# Revit family: 05-2703-14-14
name_source: partatom
category: Luminarias
revit_build: Autodesk Revit 2017 (Build: 20160225_1515(x64)
units: mm (PartAtom-declared; Revit-internal decimal feet)

## family parameters
Anfitrión = Cara
Compartido = Sí
Corte con vacíos al cargar = No
Cota de conector redondo = Diámetro de uso
Número OmniClass = 23.80.70.00
Origen de luz = No
Punto de cálculo de habitación = No
Tipo de pieza = Normal
Título OmniClass = Lighting

## types (1)
- 05-2703-14-14
    Acabado = Blanco, Opal
    CRI = 80
    Carga aparente = 0 VA
    Catálogo = Decorative
    CodigoGubimclass = 50.60.50.20
    CodigoOmniclass = 21-04 50 40
    CodigoUniclass2015 = EF_70_80
    CodigoUniformat2010 = D5040
    DescripcionGubimclass = Iluminación interior
    DescripcionOmniclass = Lighting
    DescripcionUniclass2015 = Lighting
    DescripcionUniformat2010 = Lighting
    EAN13 = 8435381423872
    Eficiencia energética = LED A++
    Elevación por defecto = 1000 mm  [stored 3.28084 ft]
    Etiqueta V/f = 100-240V/50-60Hz
    Fabricante = LEDS C4
    Familia = Lia LED 250mm
    FechaVersion = Julio 2020
    Ficha = http://files.leds-c4.com
    Fotometría = http://files.leds-c4.com
    Fuente de luz = 18xLED 6.7 630.00 lm
    IMC = http://files.leds-c4.com
    IP = IP20
    IfcExportAs = IfcLightFixture
IfcLightFixture
    IfcExportType = NOTDEFINED
    Imagen web = http://files.leds-c4.com
    LDT = http://files.leds-c4.com
    Lumenes reales (lm) = 544
    Material = Acero, Policarbonato
    Peso neto (KG) = 0.68
    Pluma comercial = http://files.leds-c4.com
    Producto descatalogado = Catalogado ES
    Rayo de luz = HORIZONTAL
    Referencia = 05-2703-14-14
    Temperatura color led (K) = Blanco cálido - 3000K
    Tender text (Castellano) = LEDS C4
Lia LED 250mm
05-2703-14-14V1

Aplique de uso interior para iluminar frontalmente y hacia abajo. 

Diseño atemporal. Muy versátil. Múltiples instalaciones. Alto rendimiento W/lm reales. Òptimo precio-rendimiento. Fácil instalación. Alta durabilidad para uso intensivo. Material estructura: Acero. Acabado estructura: Blanco. Material difusor: Policarbonato. Acabado difusor: Opal. Garantía: 5 Años.

Peso neto del producto (Kg): 0.680
Anchura o diámetro del producto (mm): 250
Altura del producto (mm): 50
Salida del producto (mm): 80

Clase 2. Prueba hilo incandescente: 960. IP: IP20. LED. Nº de portalámparas o Leds: 18. Marca del LED: SEOUL. Marca del Driver: SELF. Potencia máxima de la fuente de luz: 6.7W. Temperatura de color: Blanco cálido - 3000K. Índice de reproducción cromática: 80. Steps Mac Adam: 3. Diámetro máximo de la bombilla que admite la luminaria: 50.000h L80B20. UGR:  12.2. Riesgo fotobiológico: RG0. Flujo real (lm): 544. Flujo nominal (lm): 630. Lm/W reales: 62. Rango de voltaje/frecuencia: 100-240. Voltaje: 3. Equipo incluido: Si, electrónico. Equipo multivoltaje incluido. Potencia total: 8.8. Factor de potencia: 0.52.
    Tender text (English) = LEDS C4
Lia LED 250mm
05-2703-14-14V1

Wall light for indoor use. 

For frontal lighting and downlighting. Timeless design. Highly versatile, multiple installations. High performance W/effective lumens. Optimum price-performance. Easy instalation. High durability for intensive use. Structure material: Steel. Structure finish: White. Diffuser material: Polycarbonate. Diffuser finish: Opal. Warranty: 5 Years.

Product net weight (Kg): 0.680
Product width or diameter (mm): 250
Product height (mm): 50
Product aperture (mm): 80

Class 2. Glow wire test: 960. IP: IP20. LED. No. of lampholders or LEDs: 18. LED brand: SEOUL. Driver brand: SELF. Maximum power of light source: 6.7W. Colour temperature: LED warm-white 3000K. Colour rendering index: 80. MacAdam Steps: 3. Maximum diameter of luminaire bulb: 50.000h L80B20. UGR:  12.2. Photobiological risk: RG0. Real flux (lm): 544. Nominal flux (lm): 630. Lm/Real W: 62. Voltage and frequency range: 100-240. Voltage: 3. Gear included: Yes, electronic. Multi-voltage gear included. Total power: 8.8. Power factor: 0.52.
    Tipo = Aplique
    Vatios (W) = 8.8
    Versión = v1

note: [stored X ft] marks values corroborated as IEEE doubles in the binary element streams (Revit-internal decimal feet)
